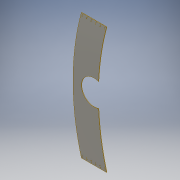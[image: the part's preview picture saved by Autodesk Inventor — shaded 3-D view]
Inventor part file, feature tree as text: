
AUTODESK INVENTOR PART (.ipt)
format: ipt  version: 2016 (Build 200138000, 138)  size: 162,816 bytes
history: native  units: mm
features: sketch x3, extrude x2, projected_geometry x2, hole x1, mirror x1
ambient origin geometry x8: Origin, YZ Plane, XZ Plane, XY Plane, X Axis, Y Axis, Z Axis, Center Point
bodies: Solid1 (feature_tree)
feature tree (9):
  extrude  "Extrusion1"  Depth=1500.0mm
  extrude  "Extrusion2"  Depth=150.0mm
  hole  "Hole2"  [1 undecoded]
  mirror  "Mirror1"
  sketch  "Sketch1"  dims[d0=1500.0mm d1=100.0mm]
  sketch  "Sketch2"  dims[d2=300.0mm d3=150.0mm]
  projected_geometry  "Projected Loop2"
  sketch  "Sketch3"  dims[d4=150.0mm d5=5.0mm d6=0.0mm d9=300.0mm d10=16.0mm d11=266.893054mm d12=60.0mm d14=53.378611mm d15=10.0mm d17=10.0mm d26=16.0mm d27=16.0mm d28=60.0mm d30=53.378611mm d31=10.0mm d33=10.0mm d35=6.2mm d36=6.0mm d37=4.0mm d38=2.0mm d39=90.0deg d40=8.0mm d41=20.594885mm d42=72.0mm d43=60.0mm d45=360.0deg d54=1.75mm d55=0.0mm]
  projected_geometry  "Projected Loop3"
note: 1 required parameter value undecoded (feature->parameter linkage not recoverable at this tier; creation-order binding heuristic only, values carry confidence <= 0.55)
